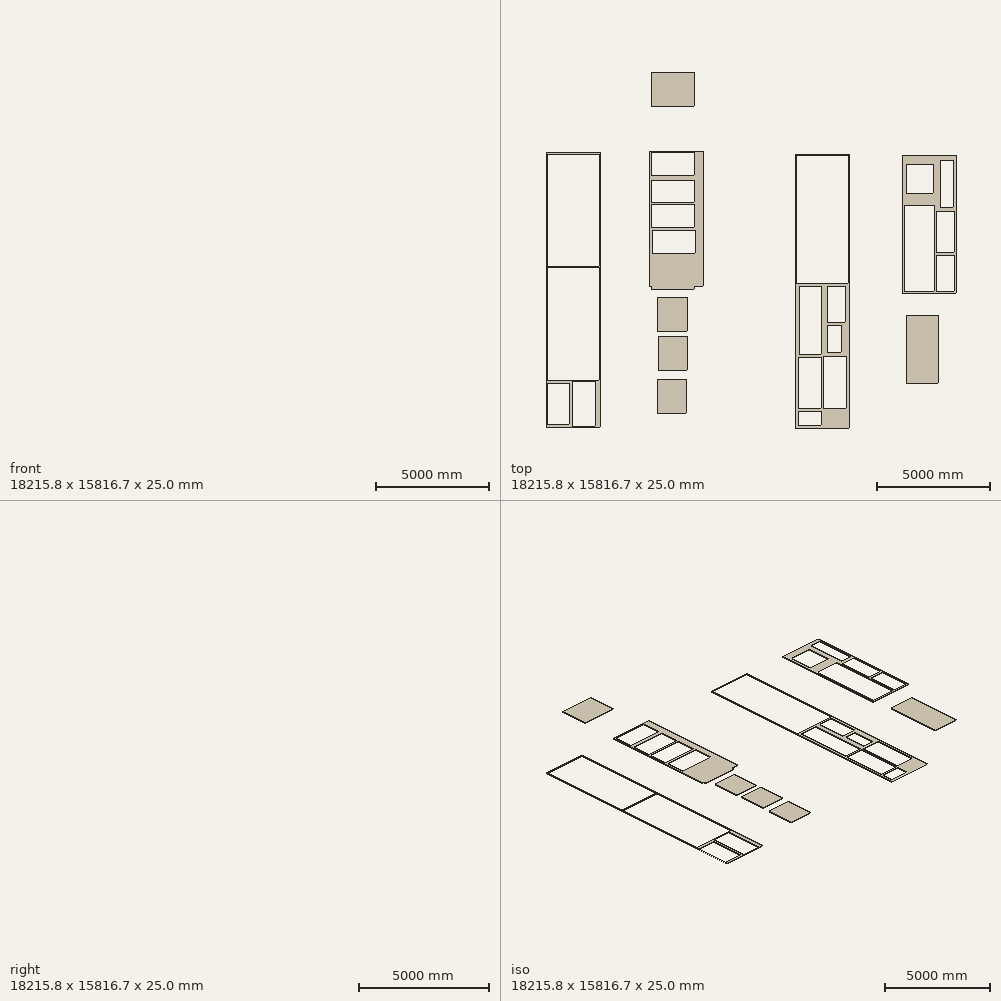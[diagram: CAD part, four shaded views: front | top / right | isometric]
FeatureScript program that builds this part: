
annotation { "Feature Type Name" : "Feature", "Feature Type Description" : "" }
export const myFeature = defineFeature(function(context is Context, id is Id, definition is map)
    precondition{}
    {
        {
            var Q0;
            Q0=qCreatedBy(makeId("Top.planeOp"),FACE);
            var sketch = newSketch(context, id + "F0", { "sketchPlane" : qUnion([Q0])});
            skLineSegment(sketch, "E0.bottom", {"start": v(-1201.68, 11008) * mm, "end": v(1198.32, 11008) * mm});
            skLineSegment(sketch, "E0.top", {"start": v(-1201.68, -1182) * mm, "end": v(1198.32, -1182) * mm});
            skLineSegment(sketch, "E0.left", {"start": v(-1201.68, 11008) * mm, "end": v(-1201.68, -1182) * mm});
            skLineSegment(sketch, "E0.right", {"start": v(1198.32, 11008) * mm, "end": v(1198.32, -1182) * mm});
            skLineSegment(sketch, "E1.bottom", {"start": v(-1148.03, 5907.82) * mm, "end": v(1151.97, 5907.82) * mm});
            skLineSegment(sketch, "E1.top", {"start": v(-1148.03, 907.82) * mm, "end": v(1151.97, 907.82) * mm});
            skLineSegment(sketch, "E1.left", {"start": v(-1148.03, 5907.82) * mm, "end": v(-1148.03, 907.82) * mm});
            skLineSegment(sketch, "E1.right", {"start": v(1151.97, 5907.82) * mm, "end": v(1151.97, 907.82) * mm});
            skLineSegment(sketch, "E2.bottom", {"start": v(-1147.15, 10952.97) * mm, "end": v(1152.85, 10952.97) * mm});
            skLineSegment(sketch, "E2.top", {"start": v(-1147.15, 5952.97) * mm, "end": v(1152.85, 5952.97) * mm});
            skLineSegment(sketch, "E2.left", {"start": v(-1147.15, 10952.97) * mm, "end": v(-1147.15, 5952.97) * mm});
            skLineSegment(sketch, "E2.right", {"start": v(1152.85, 10952.97) * mm, "end": v(1152.85, 5952.97) * mm});
            skLineSegment(sketch, "E3.bottom", {"start": v(3483.2, 6435.96) * mm, "end": v(5383.2, 6435.96) * mm});
            skLineSegment(sketch, "E3.top", {"start": v(3483.2, 4935.96) * mm, "end": v(5383.2, 4935.96) * mm});
            skLineSegment(sketch, "E3.left", {"start": v(3483.2, 6435.96) * mm, "end": v(3483.2, 4935.96) * mm});
            skLineSegment(sketch, "E3.right", {"start": v(5383.2, 6435.96) * mm, "end": v(5383.2, 4935.96) * mm});
            skLineSegment(sketch, "E4.bottom", {"start": v(-30.06, 857.11) * mm, "end": v(969.94, 857.11) * mm});
            skLineSegment(sketch, "E4.top", {"start": v(-30.06, -1142.89) * mm, "end": v(969.94, -1142.89) * mm});
            skLineSegment(sketch, "E4.left", {"start": v(-30.06, 857.11) * mm, "end": v(-30.06, -1142.89) * mm});
            skLineSegment(sketch, "E4.right", {"start": v(969.94, 857.11) * mm, "end": v(969.94, -1142.89) * mm});
            skLineSegment(sketch, "E5.bottom", {"start": v(3737.3, 928.1) * mm, "end": v(5037.3, 928.1) * mm});
            skLineSegment(sketch, "E5.top", {"start": v(3737.3, -571.9) * mm, "end": v(5037.3, -571.9) * mm});
            skLineSegment(sketch, "E5.left", {"start": v(3737.3, 928.1) * mm, "end": v(3737.3, -571.9) * mm});
            skLineSegment(sketch, "E5.right", {"start": v(5037.3, 928.1) * mm, "end": v(5037.3, -571.9) * mm});
            skLineSegment(sketch, "E6.bottom", {"start": v(3483.2, 14583.16) * mm, "end": v(5383.2, 14583.16) * mm});
            skLineSegment(sketch, "E6.top", {"start": v(3483.2, 13083.16) * mm, "end": v(5383.2, 13083.16) * mm});
            skLineSegment(sketch, "E6.left", {"start": v(3483.2, 14583.16) * mm, "end": v(3483.2, 13083.16) * mm});
            skLineSegment(sketch, "E6.right", {"start": v(5383.2, 14583.16) * mm, "end": v(5383.2, 13083.16) * mm});
            skLineSegment(sketch, "E7.bottom", {"start": v(3769.02, 2833.18) * mm, "end": v(5069.02, 2833.18) * mm});
            skLineSegment(sketch, "E7.top", {"start": v(3769.02, 1333.18) * mm, "end": v(5069.02, 1333.18) * mm});
            skLineSegment(sketch, "E7.left", {"start": v(3769.02, 2833.18) * mm, "end": v(3769.02, 1333.18) * mm});
            skLineSegment(sketch, "E7.right", {"start": v(5069.02, 2833.18) * mm, "end": v(5069.02, 1333.18) * mm});
            skLineSegment(sketch, "E8.bottom", {"start": v(3741.37, 4583.07) * mm, "end": v(5041.37, 4583.07) * mm});
            skLineSegment(sketch, "E8.top", {"start": v(3741.37, 3083.07) * mm, "end": v(5041.37, 3083.07) * mm});
            skLineSegment(sketch, "E8.left", {"start": v(3741.37, 4583.07) * mm, "end": v(3741.37, 3083.07) * mm});
            skLineSegment(sketch, "E8.right", {"start": v(5041.37, 4583.07) * mm, "end": v(5041.37, 3083.07) * mm});
            skLineSegment(sketch, "E9.bottom", {"start": v(3383.2, 11082.41) * mm, "end": v(5783.2, 11082.41) * mm});
            skLineSegment(sketch, "E9.top", {"start": v(3383.2, 5082.41) * mm, "end": v(5783.2, 5082.41) * mm});
            skLineSegment(sketch, "E9.left", {"start": v(3383.2, 11082.41) * mm, "end": v(3383.2, 5082.41) * mm});
            skLineSegment(sketch, "E9.right", {"start": v(5783.2, 11082.41) * mm, "end": v(5783.2, 5082.41) * mm});
            skLineSegment(sketch, "E10.bottom", {"start": v(3483.2, 11018.44) * mm, "end": v(5383.2, 11018.44) * mm});
            skLineSegment(sketch, "E10.top", {"start": v(3483.2, 10018.44) * mm, "end": v(5383.2, 10018.44) * mm});
            skLineSegment(sketch, "E10.left", {"start": v(3483.2, 11018.44) * mm, "end": v(3483.2, 10018.44) * mm});
            skLineSegment(sketch, "E10.right", {"start": v(5383.2, 11018.44) * mm, "end": v(5383.2, 10018.44) * mm});
            skLineSegment(sketch, "E11.bottom", {"start": v(-1174.14, 746.82) * mm, "end": v(-174.14, 746.82) * mm});
            skLineSegment(sketch, "E11.top", {"start": v(-1174.14, -1053.18) * mm, "end": v(-174.14, -1053.18) * mm});
            skLineSegment(sketch, "E11.left", {"start": v(-1174.14, 746.82) * mm, "end": v(-1174.14, -1053.18) * mm});
            skLineSegment(sketch, "E11.right", {"start": v(-174.14, 746.82) * mm, "end": v(-174.14, -1053.18) * mm});
            skLineSegment(sketch, "E12.bottom", {"start": v(3483.2, 9805.24) * mm, "end": v(5383.2, 9805.24) * mm});
            skLineSegment(sketch, "E12.top", {"start": v(3483.2, 8805.24) * mm, "end": v(5383.2, 8805.24) * mm});
            skLineSegment(sketch, "E12.left", {"start": v(3483.2, 9805.24) * mm, "end": v(3483.2, 8805.24) * mm});
            skLineSegment(sketch, "E12.right", {"start": v(5383.2, 9805.24) * mm, "end": v(5383.2, 8805.24) * mm});
            skLineSegment(sketch, "E13.bottom", {"start": v(11303.65, 3326.98) * mm, "end": v(11903.65, 3326.98) * mm});
            skLineSegment(sketch, "E13.top", {"start": v(11303.65, 2126.98) * mm, "end": v(11903.65, 2126.98) * mm});
            skLineSegment(sketch, "E13.left", {"start": v(11303.65, 3326.98) * mm, "end": v(11303.65, 2126.98) * mm});
            skLineSegment(sketch, "E13.right", {"start": v(11903.65, 3326.98) * mm, "end": v(11903.65, 2126.98) * mm});
            skLineSegment(sketch, "E14.bottom", {"start": v(16128.55, 6472.58) * mm, "end": v(16928.55, 6472.58) * mm});
            skLineSegment(sketch, "E14.top", {"start": v(16128.55, 4872.58) * mm, "end": v(16928.55, 4872.58) * mm});
            skLineSegment(sketch, "E14.left", {"start": v(16128.55, 6472.58) * mm, "end": v(16128.55, 4872.58) * mm});
            skLineSegment(sketch, "E14.right", {"start": v(16928.55, 6472.58) * mm, "end": v(16928.55, 4872.58) * mm});
            skLineSegment(sketch, "E15.bottom", {"start": v(14717, 8675.22) * mm, "end": v(16017, 8675.22) * mm});
            skLineSegment(sketch, "E15.top", {"start": v(14717, 4875.22) * mm, "end": v(16017, 4875.22) * mm});
            skLineSegment(sketch, "E15.left", {"start": v(14717, 8675.22) * mm, "end": v(14717, 4875.22) * mm});
            skLineSegment(sketch, "E15.right", {"start": v(16017, 8675.22) * mm, "end": v(16017, 4875.22) * mm});
            skLineSegment(sketch, "E16.bottom", {"start": v(11124.71, 1964.9) * mm, "end": v(12124.71, 1964.9) * mm});
            skLineSegment(sketch, "E16.top", {"start": v(11124.71, -335.1) * mm, "end": v(12124.71, -335.1) * mm});
            skLineSegment(sketch, "E16.left", {"start": v(11124.71, 1964.9) * mm, "end": v(11124.71, -335.1) * mm});
            skLineSegment(sketch, "E16.right", {"start": v(12124.71, 1964.9) * mm, "end": v(12124.71, -335.1) * mm});
            skLineSegment(sketch, "E17.bottom", {"start": v(10000.26, -483.53) * mm, "end": v(11000.26, -483.53) * mm});
            skLineSegment(sketch, "E17.top", {"start": v(10000.26, -1083.53) * mm, "end": v(11000.26, -1083.53) * mm});
            skLineSegment(sketch, "E17.left", {"start": v(10000.26, -483.53) * mm, "end": v(10000.26, -1083.53) * mm});
            skLineSegment(sketch, "E17.right", {"start": v(11000.26, -483.53) * mm, "end": v(11000.26, -1083.53) * mm});
            skLineSegment(sketch, "E18.bottom", {"start": v(11283.57, 5092.81) * mm, "end": v(12083.57, 5092.81) * mm});
            skLineSegment(sketch, "E18.top", {"start": v(11283.57, 3492.81) * mm, "end": v(12083.57, 3492.81) * mm});
            skLineSegment(sketch, "E18.left", {"start": v(11283.57, 5092.81) * mm, "end": v(11283.57, 3492.81) * mm});
            skLineSegment(sketch, "E18.right", {"start": v(12083.57, 5092.81) * mm, "end": v(12083.57, 3492.81) * mm});
            skLineSegment(sketch, "E19.bottom", {"start": v(10003.13, 1939.44) * mm, "end": v(11003.13, 1939.44) * mm});
            skLineSegment(sketch, "E19.top", {"start": v(10003.13, -360.56) * mm, "end": v(11003.13, -360.56) * mm});
            skLineSegment(sketch, "E19.left", {"start": v(10003.13, 1939.44) * mm, "end": v(10003.13, -360.56) * mm});
            skLineSegment(sketch, "E19.right", {"start": v(11003.13, 1939.44) * mm, "end": v(11003.13, -360.56) * mm});
            skLineSegment(sketch, "E20.bottom", {"start": v(16299.3, 10694.84) * mm, "end": v(16899.3, 10694.84) * mm});
            skLineSegment(sketch, "E20.top", {"start": v(16299.3, 8594.84) * mm, "end": v(16899.3, 8594.84) * mm});
            skLineSegment(sketch, "E20.left", {"start": v(16299.3, 10694.84) * mm, "end": v(16299.3, 8594.84) * mm});
            skLineSegment(sketch, "E20.right", {"start": v(16899.3, 10694.84) * mm, "end": v(16899.3, 8594.84) * mm});
            skLineSegment(sketch, "E21.bottom", {"start": v(10022.5, 5061.65) * mm, "end": v(11022.5, 5061.65) * mm});
            skLineSegment(sketch, "E21.top", {"start": v(10022.5, 2061.65) * mm, "end": v(11022.5, 2061.65) * mm});
            skLineSegment(sketch, "E21.left", {"start": v(10022.5, 5061.65) * mm, "end": v(10022.5, 2061.65) * mm});
            skLineSegment(sketch, "E21.right", {"start": v(11022.5, 5061.65) * mm, "end": v(11022.5, 2061.65) * mm});
            skLineSegment(sketch, "E22.bottom", {"start": v(9912.84, 10902.4) * mm, "end": v(12212.84, 10902.4) * mm});
            skLineSegment(sketch, "E22.top", {"start": v(9912.84, 5202.4) * mm, "end": v(12212.84, 5202.4) * mm});
            skLineSegment(sketch, "E22.left", {"start": v(9912.84, 10902.4) * mm, "end": v(9912.84, 5202.4) * mm});
            skLineSegment(sketch, "E22.right", {"start": v(12212.84, 10902.4) * mm, "end": v(12212.84, 5202.4) * mm});
            skLineSegment(sketch, "E23.bottom", {"start": v(14798.67, 10493.3) * mm, "end": v(15998.67, 10493.3) * mm});
            skLineSegment(sketch, "E23.top", {"start": v(14798.67, 9193.3) * mm, "end": v(15998.67, 9193.3) * mm});
            skLineSegment(sketch, "E23.left", {"start": v(14798.67, 10493.3) * mm, "end": v(14798.67, 9193.3) * mm});
            skLineSegment(sketch, "E23.right", {"start": v(15998.67, 10493.3) * mm, "end": v(15998.67, 9193.3) * mm});
            skLineSegment(sketch, "E24.bottom", {"start": v(16122.29, 8405.61) * mm, "end": v(16922.29, 8405.61) * mm});
            skLineSegment(sketch, "E24.top", {"start": v(16122.29, 6605.61) * mm, "end": v(16922.29, 6605.61) * mm});
            skLineSegment(sketch, "E24.left", {"start": v(16122.29, 8405.61) * mm, "end": v(16122.29, 6605.61) * mm});
            skLineSegment(sketch, "E24.right", {"start": v(16922.29, 8405.61) * mm, "end": v(16922.29, 6605.61) * mm});
            skLineSegment(sketch, "E25.bottom", {"start": v(14796.11, 3768.82) * mm, "end": v(16196.11, 3768.82) * mm});
            skLineSegment(sketch, "E25.top", {"start": v(14796.11, 768.82) * mm, "end": v(16196.11, 768.82) * mm});
            skLineSegment(sketch, "E25.left", {"start": v(14796.11, 3768.82) * mm, "end": v(14796.11, 768.82) * mm});
            skLineSegment(sketch, "E25.right", {"start": v(16196.11, 3768.82) * mm, "end": v(16196.11, 768.82) * mm});
            skLineSegment(sketch, "E26.bottom", {"start": v(9873.69, 10956.5) * mm, "end": v(12273.69, 10956.5) * mm});
            skLineSegment(sketch, "E26.top", {"start": v(9873.69, -1233.5) * mm, "end": v(12273.69, -1233.5) * mm});
            skLineSegment(sketch, "E26.left", {"start": v(9873.69, 10956.5) * mm, "end": v(9873.69, -1233.5) * mm});
            skLineSegment(sketch, "E26.right", {"start": v(12273.69, 10956.5) * mm, "end": v(12273.69, -1233.5) * mm});
            skLineSegment(sketch, "E27.bottom", {"start": v(14614.14, 10883.56) * mm, "end": v(17014.14, 10883.56) * mm});
            skLineSegment(sketch, "E27.top", {"start": v(14614.14, 4783.56) * mm, "end": v(17014.14, 4783.56) * mm});
            skLineSegment(sketch, "E27.left", {"start": v(14614.14, 10883.56) * mm, "end": v(14614.14, 4783.56) * mm});
            skLineSegment(sketch, "E27.right", {"start": v(17014.14, 10883.56) * mm, "end": v(17014.14, 4783.56) * mm});
            skLineSegment(sketch, "E28.bottom", {"start": v(3484.12, 8698.73) * mm, "end": v(5384.12, 8698.73) * mm});
            skLineSegment(sketch, "E28.top", {"start": v(3484.12, 7698.73) * mm, "end": v(5384.12, 7698.73) * mm});
            skLineSegment(sketch, "E28.left", {"start": v(3484.12, 8698.73) * mm, "end": v(3484.12, 7698.73) * mm});
            skLineSegment(sketch, "E28.right", {"start": v(5384.12, 8698.73) * mm, "end": v(5384.12, 7698.73) * mm});
            skLineSegment(sketch, "E29.bottom", {"start": v(3514.27, 7551) * mm, "end": v(5414.27, 7551) * mm});
            skLineSegment(sketch, "E29.top", {"start": v(3514.27, 6551) * mm, "end": v(5414.27, 6551) * mm});
            skLineSegment(sketch, "E29.left", {"start": v(3514.27, 7551) * mm, "end": v(3514.27, 6551) * mm});
            skLineSegment(sketch, "E29.right", {"start": v(5414.27, 7551) * mm, "end": v(5414.27, 6551) * mm});
            skSolve(sketch);
        }
        {
            var Q0;
            Q0 = qSketchRegion(id + "F0", true);
            extrude(context, id + "F1", {"entities" : qUnion([Q0]), "depth" : 25 * mm, "offsetDistance" : 25 * mm});
        }
    });
